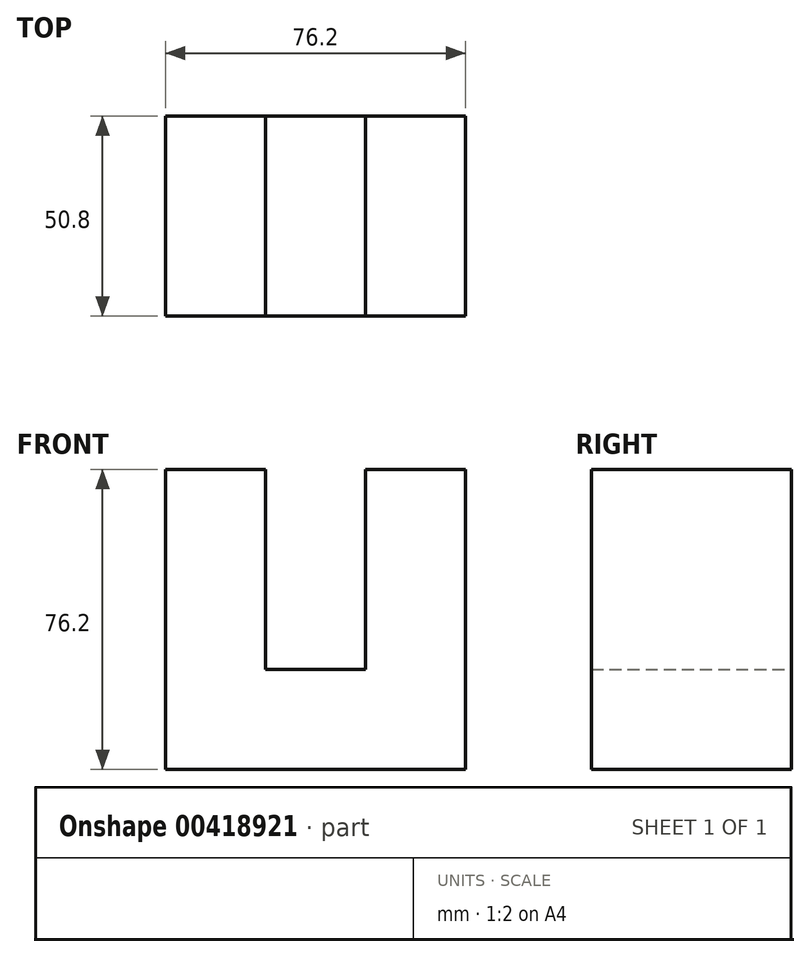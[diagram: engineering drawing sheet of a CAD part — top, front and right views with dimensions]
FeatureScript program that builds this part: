
annotation { "Feature Type Name" : "Feature", "Feature Type Description" : "" }
export const myFeature = defineFeature(function(context is Context, id is Id, definition is map)
    precondition{}
    {
        {
            var Q0;
            Q0=qCreatedBy(makeId("Front.planeOp"),FACE);
            var sketch = newSketch(context, id + "F0", { "sketchPlane" : qUnion([Q0])});
            skLineSegment(sketch, "E0", {"start": v(0, 76.2) * mm, "end": v(0, 0) * mm});
            skLineSegment(sketch, "E1", {"start": v(0, 0) * mm, "end": v(-76.2, 0) * mm});
            skLineSegment(sketch, "E2", {"start": v(-76.2, 0) * mm, "end": v(-76.2, 76.2) * mm});
            skLineSegment(sketch, "E3", {"start": v(-76.2, 76.2) * mm, "end": v(-50.8, 76.2) * mm});
            skLineSegment(sketch, "E4", {"start": v(-50.8, 76.2) * mm, "end": v(-50.8, 25.4) * mm});
            skLineSegment(sketch, "E5", {"start": v(-50.8, 25.4) * mm, "end": v(-25.4, 25.4) * mm});
            skLineSegment(sketch, "E6", {"start": v(-25.4, 25.4) * mm, "end": v(-25.4, 76.2) * mm});
            skLineSegment(sketch, "E7", {"start": v(-25.4, 76.2) * mm, "end": v(0, 76.2) * mm});
            skSolve(sketch);
        }
        {
            var Q0;
            Q0=makeQuery(id+"F0.imprint","IMPRINT",FACE,{"disambiguationData":[TD([[makeQuery(id+"F0.imprint","IMPRINT",EDGE,{"derivedFrom":sQuery(id+"F0.wireOp",EDGE,"E0")}),-1.0]])]});
            extrude(context, id + "F1", {"entities" : qUnion([Q0]), "depth" : 50.8 * mm});
        }
    });
